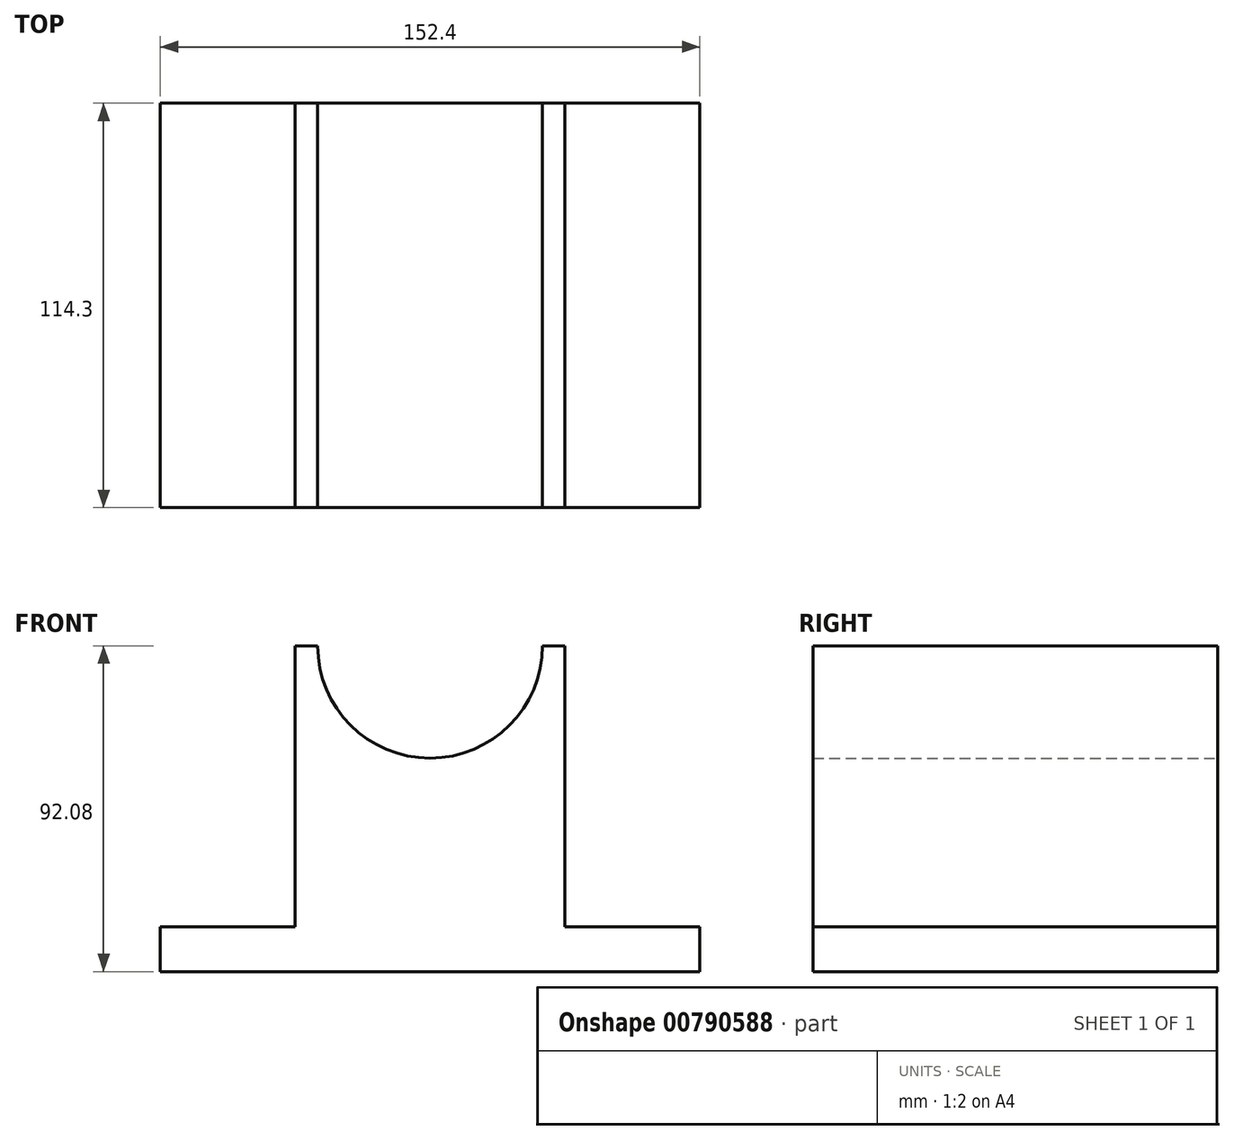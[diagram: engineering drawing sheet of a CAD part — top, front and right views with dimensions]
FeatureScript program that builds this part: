
annotation { "Feature Type Name" : "Feature", "Feature Type Description" : "" }
export const myFeature = defineFeature(function(context is Context, id is Id, definition is map)
    precondition{}
    {
        {
            var Q0;
            Q0=qCreatedBy(makeId("Front.planeOp"),FACE);
            var sketch = newSketch(context, id + "F0", { "sketchPlane" : qUnion([Q0])});
            skLineSegment(sketch, "E0", {"start": v(0, 0) * mm, "end": v(-76.2, 0) * mm});
            skLineSegment(sketch, "E1", {"start": v(0, 0) * mm, "end": v(76.2, 0) * mm});
            skLineSegment(sketch, "E2", {"start": v(76.2, 0) * mm, "end": v(76.2, 12.7) * mm});
            skLineSegment(sketch, "E3", {"start": v(-76.2, 0) * mm, "end": v(-76.2, 12.7) * mm});
            skLineSegment(sketch, "E4", {"start": v(-76.2, 12.7) * mm, "end": v(-38.1, 12.7) * mm});
            skLineSegment(sketch, "E5", {"start": v(76.2, 12.7) * mm, "end": v(38.1, 12.7) * mm});
            skLineSegment(sketch, "E6", {"start": v(-38.1, 12.7) * mm, "end": v(-38.1, 92.08) * mm});
            skLineSegment(sketch, "E7", {"start": v(38.1, 12.7) * mm, "end": v(38.1, 92.08) * mm});
            skLineSegment(sketch, "E8", {"start": v(-38.1, 92.08) * mm, "end": v(-31.75, 92.08) * mm});
            skLineSegment(sketch, "E9", {"start": v(38.1, 92.08) * mm, "end": v(31.75, 92.08) * mm});
            skArc(sketch, "E10", {"start": v(-31.75, 92.08) * mm, "mid": v(0, 60.33) * mm, "end": v(31.75, 92.08) * mm});
            skSolve(sketch);
        }
        {
            var Q0;
            Q0 = qSketchRegion(id + "F0", true);
            extrude(context, id + "F1", {"entities" : qUnion([Q0]), "depth" : 114.3 * mm, "offsetDistance" : 25.4 * mm});
        }
    });
